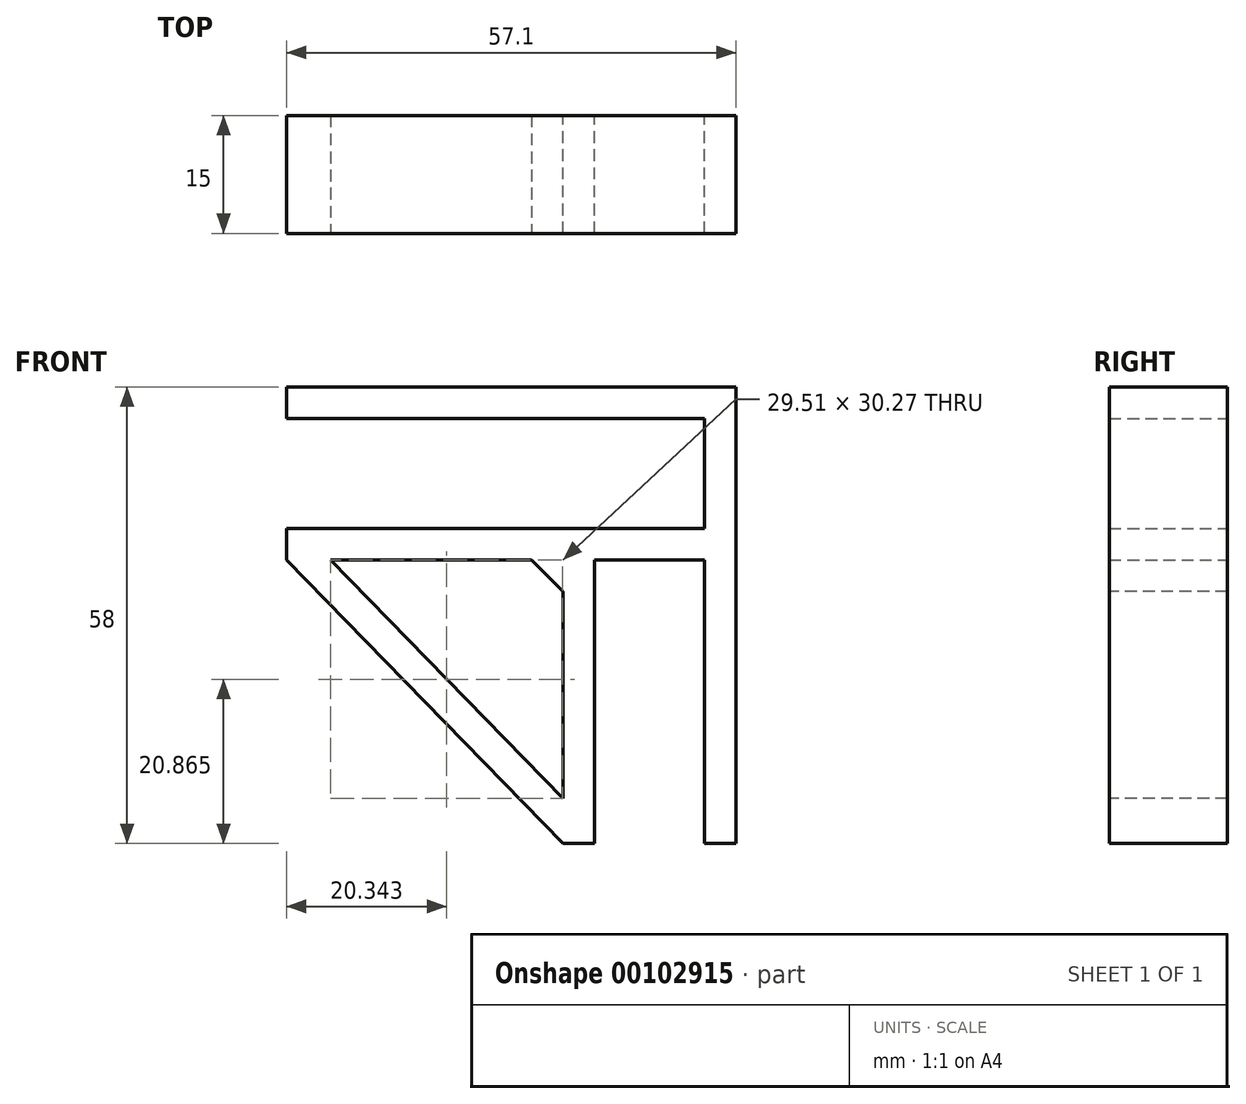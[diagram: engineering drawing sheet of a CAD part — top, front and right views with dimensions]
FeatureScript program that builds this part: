
annotation { "Feature Type Name" : "Feature", "Feature Type Description" : "" }
export const myFeature = defineFeature(function(context is Context, id is Id, definition is map)
    precondition{}
    {
        {
            var Q0;
            Q0=qCreatedBy(makeId("Front.planeOp"),FACE);
            var sketch = newSketch(context, id + "F0", { "sketchPlane" : qUnion([Q0])});
            skLineSegment(sketch, "E0.bottom", {"start": v(-42.04, 0) * mm, "end": v(-110, 0) * mm});
            skLineSegment(sketch, "E0.top", {"start": v(-42.04, 14) * mm, "end": v(-110, 14) * mm});
            skLineSegment(sketch, "E0.left", {"start": v(-42.04, 0) * mm, "end": v(-42.04, 14) * mm});
            skLineSegment(sketch, "E0.right", {"start": v(-110, 0) * mm, "end": v(-110, 14) * mm});
            skLineSegment(sketch, "E1.bottom", {"start": v(-42.04, -4) * mm, "end": v(-56.04, -4) * mm});
            skLineSegment(sketch, "E1.left", {"start": v(-42.04, -4) * mm, "end": v(-42.04, -40) * mm});
            skLineSegment(sketch, "E1.right", {"start": v(-56.04, -4) * mm, "end": v(-56.04, -40) * mm});
            skLineSegment(sketch, "E2", {"start": v(-95.14, 18) * mm, "end": v(-42.04, 18) * mm});
            skPoint(sketch, "E3.center.orphan", {"position": v(-42.04, 7) * mm});
            skLineSegment(sketch, "E4", {"start": v(-42.04, 18) * mm, "end": v(-38.04, 18) * mm});
            skLineSegment(sketch, "E5", {"start": v(-38.04, 18) * mm, "end": v(-38.04, -40) * mm});
            skLineSegment(sketch, "E6", {"start": v(-95.14, 18) * mm, "end": v(-95.14, 14) * mm});
            skLineSegment(sketch, "E7", {"start": v(-60.04, -40) * mm, "end": v(-38.04, -40) * mm});
            skLineSegment(sketch, "E8", {"start": v(-95.14, -4) * mm, "end": v(-95.14, 0) * mm});
            skLineSegment(sketch, "E9", {"start": v(-95.14, -4) * mm, "end": v(-60.04, -40) * mm});
            skSolve(sketch);
        }
        {
            var Q0;
            {var subQ3=sQuery(id+"F0.wireOp",EDGE,"E0.left");Q0=makeQuery(id+"F0.imprint","IMPRINT",FACE,{"disambiguationData":[TD([[makeQuery(id+"F0.imprint","IMPRINT",EDGE,{"derivedFrom":subQ3}),-1.0]])]});}
            extrude(context, id + "F1", {"entities" : qUnion([Q0]), "endBound" : BoundingType.SYMMETRIC, "depth" : 15 * mm});
        }
        {
            var Q0;
            Q0=makeQuery(id+"F1.opExtrude","CAP_FACE",FACE,{"disambiguationData":[OSD([sQuery(id+"F0.wireOp",EDGE,"E0.bottom"),sQuery(id+"F0.wireOp",EDGE,"E0.top"),sQuery(id+"F0.wireOp",EDGE,"E0.left"),sQuery(id+"F0.wireOp",EDGE,"E1.bottom"),sQuery(id+"F0.wireOp",EDGE,"E1.left"),sQuery(id+"F0.wireOp",EDGE,"E2"),sQuery(id+"F0.wireOp",EDGE,"E1.right"),sQuery(id+"F0.wireOp",EDGE,"1G9kRUcp-9Ku8-VOWx-SY3P-BoGxEr0XXavj"),sQuery(id+"F0.wireOp",EDGE,"E4"),sQuery(id+"F0.wireOp",EDGE,"E5"),sQuery(id+"F0.wireOp",EDGE,"E6"),sQuery(id+"F0.wireOp",EDGE,"E7"),sQuery(id+"F0.wireOp",EDGE,"E8")])],"isStart":false});
            var sketch = newSketch(context, id + "F2", { "sketchPlane" : qUnion([Q0])});
            skLineSegment(sketch, "E10", {"start": v(-64.04, -4) * mm, "end": v(-89.55, -4) * mm});
            skLineSegment(sketch, "E11", {"start": v(-60.04, -8) * mm, "end": v(-60.04, -34.27) * mm});
            skLineSegment(sketch, "E12", {"start": v(-89.55, -4) * mm, "end": v(-60.04, -34.27) * mm});
            skLineSegment(sketch, "E13", {"start": v(-64.04, -4) * mm, "end": v(-60.04, -8) * mm});
            skPoint(sketch, "E14.start.orphan", {"position": v(-56.04, -4) * mm});
            skSolve(sketch);
        }
        {
            var Q0;
            Q0=makeQuery(id+"F2.imprint","IMPRINT",FACE,{"disambiguationData":[TD([[makeQuery(id+"F2.imprint","IMPRINT",EDGE,{"derivedFrom":sQuery(id+"F2.wireOp",EDGE,"E10")}),1.0]])]});
            var Q1;
            Q1=makeQuery(id+"F1.opExtrude","CAP_FACE",FACE,{"disambiguationData":[OSD([sQuery(id+"F0.wireOp",EDGE,"E0.bottom"),sQuery(id+"F0.wireOp",EDGE,"E0.top"),sQuery(id+"F0.wireOp",EDGE,"E0.left"),sQuery(id+"F0.wireOp",EDGE,"E1.bottom"),sQuery(id+"F0.wireOp",EDGE,"E1.left"),sQuery(id+"F0.wireOp",EDGE,"E2"),sQuery(id+"F0.wireOp",EDGE,"E1.right"),sQuery(id+"F0.wireOp",EDGE,"1G9kRUcp-9Ku8-VOWx-SY3P-BoGxEr0XXavj"),sQuery(id+"F0.wireOp",EDGE,"E4"),sQuery(id+"F0.wireOp",EDGE,"E5"),sQuery(id+"F0.wireOp",EDGE,"E6"),sQuery(id+"F0.wireOp",EDGE,"E7"),sQuery(id+"F0.wireOp",EDGE,"E8")])],"isStart":true});
            extrude(context, id + "F3", {"entities" : qUnion([Q0, Q1]), "operationType" : NewBodyOperationType.REMOVE, "endBound" : BoundingType.THROUGH_ALL, "oppositeDirection" : true, "depth" : 25 * mm});
        }
    });
